# Revit family: 0045754
name_source: partatom
category: Lighting Fixtures
revit_build: Autodesk Revit 2017 (Build: 20190507_1515(x64)
units: mm (PartAtom-declared; Revit-internal decimal feet)

## family parameters
Cut with Voids When Loaded = No
Host = Face
Light Source = Yes
OmniClass Number = 23.80.70.00
OmniClass Title = Lighting
Part Type = Normal
Room Calculation Point = No
Round Connector Dimension = Use Diameter
Shared = No

## types (6) — shared parameters
Assembly Code = D5020200
AssetType = Fixed
BODY_END_SYL = 264 mm  [stored 0.866142 ft]
BODY_ST_SYL = 204 mm
BRACKET1_END_SYL = 204 mm
BRACKET1_ST_SYL = 244 mm  [stored 0.800525 ft]
CABLE_D_SYL = 23 mm
ClassificationName = Uniclass2015
ClassificationValue = EF_70_80
Color Filter = 16777215
Default Elevation = 1219 mm
Dimming Lamp Color Temperature Shift = <None>
DocumentationLiterature = http://www.sylvania-lighting.com
ElectricShockClassification = Class II
Emit Shape Visible in Rendering = No
Emit from Circle Diameter = 610 mm
IfcExportAs = IfcLightFixtureType
IfcExportType = IfcLightFixtureType
ImpactProtectionIndex = IK08
IngressProtection = IP65
Keynote = 16500
L3_SYL = 7 mm  [stored 0.0229659 ft]
LAMP_END_SYL = 228 mm
LAMP_L1_SYL = 577 mm
LAMP_ST_SYL = -866 mm
LUM_D1_SYL = 38 mm  [stored 0.124672 ft]
LUM_H_SYL = 50 mm  [stored 0.164042 ft]
LUM_LENGHT1500_SYL = No
LUM_W_SYL = 40 mm
L_CABLE_SYL = 47 mm
Lamp = LED
LampColourRenderingIndex = 80
LampMacAdamStep = 5
LampsType = LED
Manufacturer = Feilo Sylvania
ManufacturerName = Feilo Sylvania
Material_1_SYL = <By Category>
Material_2_SYL = <By Category>
Material_3_SYL = <By Category>
Material_4_SYL = <By Category>
PowerFactor = 0.9
Tilt Angle = -90.00°
Type Image = <None>
URL = http://www.sylvania-lighting.com
Voltage = 0 V
zero-valued in all types: Cost, LUM_D2_SYL

## per-type parameters (varying)
| type | Apparent Load | Description | LampColourTemperature | LampNominalLuminous | LightOutputRatio | LuminousEfficacy | Material | Model | ModelNumber | ModelReference | Name | NominalDepth | NominalHeight | NominalLength | Photometric Web File | PowerConsumption | TypeName | Weight |
| 0045753 ST E BATTEN 1500 IP65 6000LM 830 | 42 VA |  | 3000 K | 6000 lm |  | 143 lm/W | pc polycarbonate housing, pc polycarbonate diffuser | START eco Batten 1500 IP65 6000lm 830 | 0045753 | START eco Batten 1500 IP65 6000lm 830 | START eco Batten 1500 IP65 6000lm 830 | 80 mm  [stored 0.262467 ft] | 55 mm  [stored 0.180446 ft] | 1560 mm  [stored 5.11811 ft] | 0045753.ies | 42 W | START eco Batten 1500 IP65 6000lm 830 | 13.8 kg |
| 0045750 ST E BATTEN 1200 IP65 5200LM 840 | 36 VA |  | 4000 K | 5200 lm |  | 144 lm/W | pc polycarbonate housing, pc polycarbonate diffuser | START eco Batten  1200 IP65 5200lm 840 | 0045750 | START eco Batten  1200 IP65 5200lm 840 | START eco Batten  1200 IP65 5200lm 840 | 80 mm  [stored 0.262467 ft] | 55 mm  [stored 0.180446 ft] | 1260 mm  [stored 4.13386 ft] | 0045750.ies | 36 W | START eco Batten  1200 IP65 5200lm 840 | 7.02 kg |
| 0045749 ST E BATTEN 1200 IP65 5200LM 830 | 36 VA |  | 3000 K | 5200 lm |  | 144 lm/W | pc polycarbonate housing, pc polycarbonate diffuser | START eco Batten 1200 IP65 5200lm 830 | 0045749 | START eco Batten 1200 IP65 5200lm 830 | START eco Batten 1200 IP65 5200lm 830 | 80 mm  [stored 0.262467 ft] | 55 mm  [stored 0.180446 ft] | 1260 mm  [stored 4.13386 ft] | 0045749.ies | 36 W | START eco Batten 1200 IP65 5200lm 830 | 7.02 kg |
| 0045416 ST E BATTEN NEO 1500 IP65 6000LM 865 ME | 48 VA | The new upgraded Start eco Batten IP65 (upgraded version of Batten LED LINK) is a versatile range of slimline LED waterproof luminaires that provide an ideal solution for interior and exterior applications such as workshops, garages and outdoor covered spaces. The design allows the luminaire to be easily linked to another luminaire through an IP65 rated connector. The product can be a slimline replacement for single and twin 36W/58W fluorescent waterproof battens.Polycarbonate housing and diffuser, 5520 lm, 48 W, 115 lm/W, 3000 K, drive current 300 mA, non dimmable, CRI 80, IP65, IK08, Class II, nominal average lifetime (h): 30000, 1500 mm x 80 mm x 53.6 mm, energy class: A++ A+ A. | 6500 K | 6000 lm | 100 | 125 lm/W |  | START eco Batten NEO 1500 IP65 6000lm 865 ME | 0045416 | START eco Batten NEO 1500 IP65 6000lm 865 ME | START eco Batten NEO 1500 IP65 6000lm 865 ME | 80 mm  [stored 0.262467 ft] | 54 mm | 1500 mm  [stored 4.92126 ft] | 0045416.ies | 48 W | START eco Batten NEO 1500 IP65 6000lm 865 ME | 12.213 kg |
| 0045414 ST E BATTEN NEO 1200 IP65 5200LM 865 ME | 36 VA | The new upgraded Start eco Batten IP65 (upgraded version of Batten LED LINK) is a versatile range of slimline LED waterproof luminaires that provide an ideal solution for interior and exterior applications such as workshops, garages and outdoor covered spaces. The design allows the luminaire to be easily linked to another luminaire through an IP65 rated connector. The product can be a slimline replacement for single and twin 36W/58W fluorescent waterproof battens.Polycarbonate housing and diffuser, 2500 lm, 20 W, 125 lm/W, 4000 K, drive current 130 mA, non dimmable, CRI 80, IP65, IK08, Class II, nominal average lifetime (h): 30000, 1200 mm x 42 mm x 52.8 mm, energy class: A++ A+ A. | 6500 K | 5200 lm | 100 | 144 lm/W |  | START eco Batten NEO 1200 IP65 5200lm 865 ME | 0045414 | START eco Batten NEO 1200 IP65 5200lm 865 ME | START eco Batten NEO 1200 IP65 5200lm 865 ME | 44 mm  [stored 0.144357 ft] | 53 mm | 1200 mm | 0045414.ies | 36 W | START eco Batten NEO 1200 IP65 5200lm 865 ME | 13.368 kg |
| 0045754 ST E BATTEN 1500 IP65 6000LM 840 | 42 VA |  | 4000 K | 6000 lm |  | 143 lm/W | pc polycarbonate housing, pc polycarbonate diffuser | START eco Batten 1500 IP65 6000lm 840 | 0045754 | START eco Batten 1500 IP65 6000lm 840 | START eco Batten 1500 IP65 6000lm 840 | 80 mm  [stored 0.262467 ft] | 55 mm  [stored 0.180446 ft] | 1560 mm  [stored 5.11811 ft] | 0045754.ies | 42 W | START eco Batten 1500 IP65 6000lm 840 | 8.28 kg |

note: [stored X ft] marks values corroborated as IEEE doubles in the binary element streams (Revit-internal decimal feet)

## geometry (parser evidence)
native form markers: Sweep x1
no freeform markers — native parametric forms only
